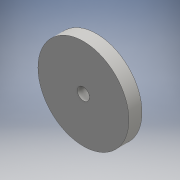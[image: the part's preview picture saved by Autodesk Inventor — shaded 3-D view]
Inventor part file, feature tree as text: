
AUTODESK INVENTOR PART (.ipt)
format: ipt  version: 2016 (Build 200138000, 138)  size: 94,208 bytes
history: native  units: mm
features: extrude x2, sketch x2
ambient origin geometry x8: Origin, YZ Plane, XZ Plane, XY Plane, X Axis, Y Axis, Z Axis, Center Point
bodies: Solid1 (feature_tree)
feature tree (4):
  extrude  "Extrusion1"  Depth=13.0mm TaperAngle=0.0deg
  extrude  "Extrusion2"  Depth=13.0mm TaperAngle=0.0deg
  sketch  "Sketch1"  dims[d0=90.0mm d1=13.0mm d2=0.0mm]
  sketch  "Sketch2"  dims[d3=12.0mm d4=13.0mm d5=0.0mm]
